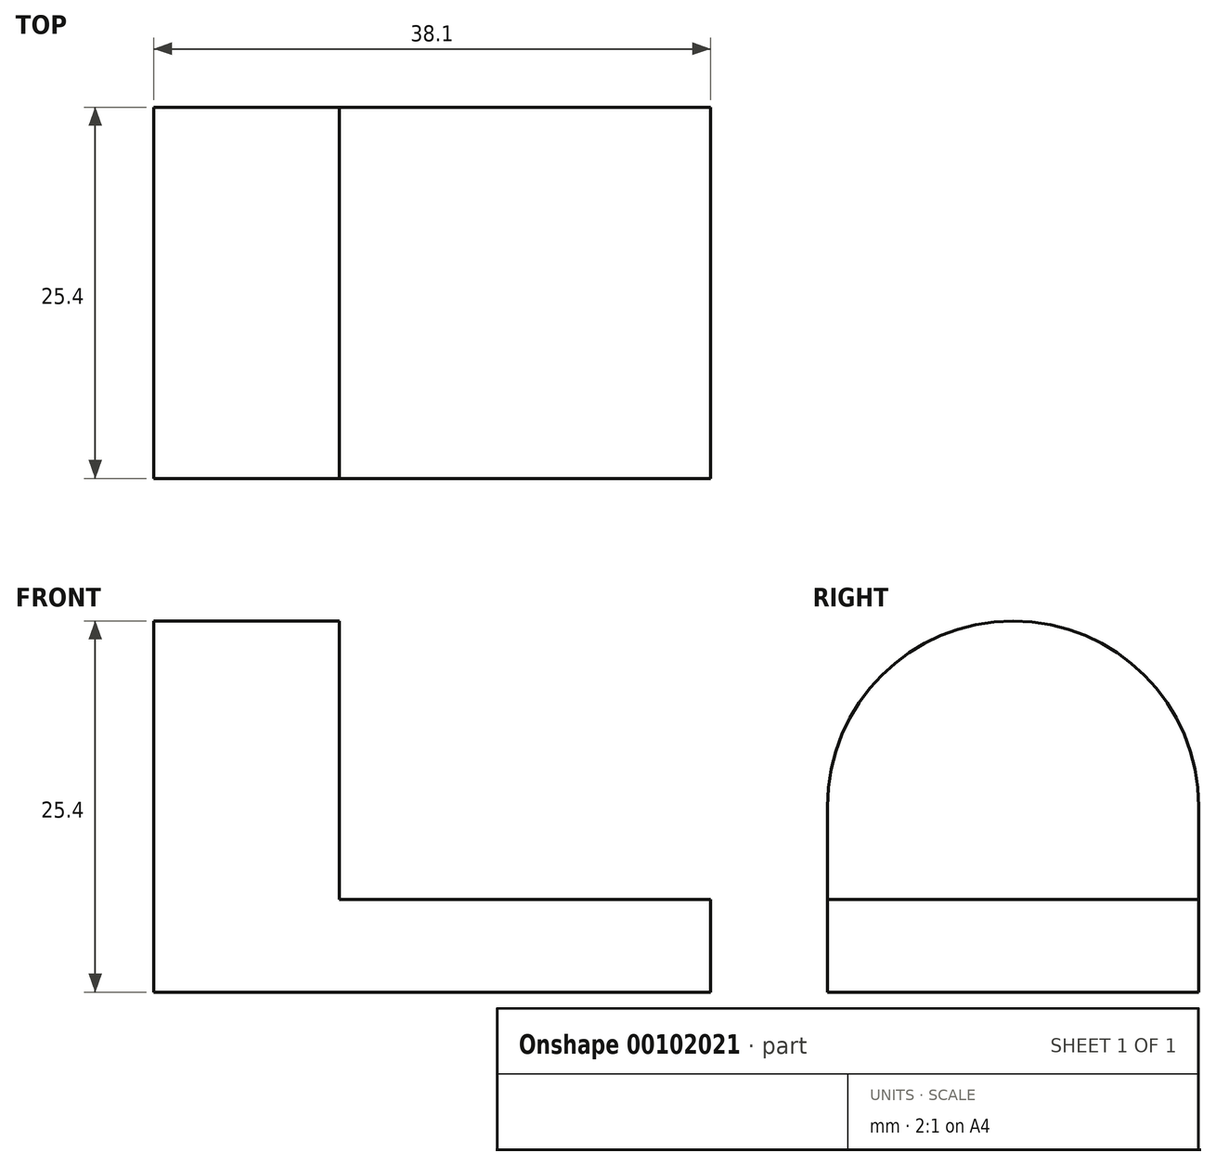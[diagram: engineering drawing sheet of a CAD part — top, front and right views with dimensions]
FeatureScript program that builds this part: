
annotation { "Feature Type Name" : "Feature", "Feature Type Description" : "" }
export const myFeature = defineFeature(function(context is Context, id is Id, definition is map)
    precondition{}
    {
        {
            var Q0;
            Q0=qCreatedBy(makeId("Top.planeOp"),FACE);
            var sketch = newSketch(context, id + "F0", { "sketchPlane" : qUnion([Q0])});
            skLineSegment(sketch, "E0", {"start": v(0, 0) * mm, "end": v(38.1, 0) * mm});
            skLineSegment(sketch, "E1", {"start": v(38.1, 0) * mm, "end": v(38.1, 25.4) * mm});
            skLineSegment(sketch, "E2", {"start": v(38.1, 25.4) * mm, "end": v(0, 25.4) * mm});
            skLineSegment(sketch, "E3", {"start": v(0, 25.4) * mm, "end": v(0, 0) * mm});
            skSolve(sketch);
        }
        {
            var Q0;
            Q0 = qSketchRegion(id + "F0", true);
            extrude(context, id + "F1", {"entities" : qUnion([Q0]), "depth" : 25.4 * mm});
        }
        {
            var Q0;
            Q0=makeQuery(id+"F1.opExtrude","SWEPT_FACE",FACE,{"disambiguationData":[OSD([sQuery(id+"F0.wireOp",EDGE,"E1")])]});
            var sketch = newSketch(context, id + "F2", { "sketchPlane" : qUnion([Q0])});
            skLineSegment(sketch, "E4", {"start": v(0, 0) * mm, "end": v(0, 6.35) * mm});
            skLineSegment(sketch, "E5", {"start": v(0, 6.35) * mm, "end": v(25.4, 6.35) * mm});
            skLineSegment(sketch, "E6", {"start": v(25.4, 6.35) * mm, "end": v(25.4, 0) * mm});
            skLineSegment(sketch, "E7", {"start": v(25.4, 0) * mm, "end": v(0, 0) * mm});
            skSolve(sketch);
        }
        {
            var Q0;
            {var subQ0=sQuery(id+"F2.wireOp",EDGE,"E5");Q0=makeQuery(id+"F2.imprint","IMPRINT",FACE,{"disambiguationData":[TD([[makeQuery(id+"F2.imprint","IMPRINT",EDGE,{"derivedFrom":subQ0}),1.0]])]});}
            extrude(context, id + "F3", {"entities" : qUnion([Q0]), "operationType" : NewBodyOperationType.REMOVE, "oppositeDirection" : true, "depth" : 25.4 * mm});
        }
        {
            var Q0;
            Q0=makeQuery(id+"F1.opExtrude","CAP_FACE",FACE,{"disambiguationData":[OSD([sQuery(id+"F0.wireOp",EDGE,"E0"),sQuery(id+"F0.wireOp",EDGE,"E1"),sQuery(id+"F0.wireOp",EDGE,"E2"),sQuery(id+"F0.wireOp",EDGE,"E3")])],"isStart":false});
            extrude(context, id + "F4", {"entities" : qUnion([Q0]), "operationType" : NewBodyOperationType.REMOVE, "oppositeDirection" : true, "depth" : 12.7 * mm});
        }
        {
            var Q0;
            Q0=makeQuery(id+"F1.opExtrude","SWEPT_FACE",FACE,{"disambiguationData":[OSD([sQuery(id+"F0.wireOp",EDGE,"E3")])]});
            var sketch = newSketch(context, id + "F5", { "sketchPlane" : qUnion([Q0])});
            skArc(sketch, "E8", {"start": v(0, 12.7) * mm, "mid": v(-12.7, 25.4) * mm, "end": v(-25.4, 12.7) * mm});
            skSolve(sketch);
        }
        {
            var Q0;
            Q0=makeQuery(id+"F5.imprint","IMPRINT",FACE,{"disambiguationData":[TD([[makeQuery(id+"F5.imprint","IMPRINT",EDGE,{"derivedFrom":sQuery(id+"F5.wireOp",EDGE,"E8")}),1.0]])]});
            extrude(context, id + "F6", {"entities" : qUnion([Q0]), "operationType" : NewBodyOperationType.ADD, "oppositeDirection" : true, "depth" : 12.7 * mm});
        }
    });
